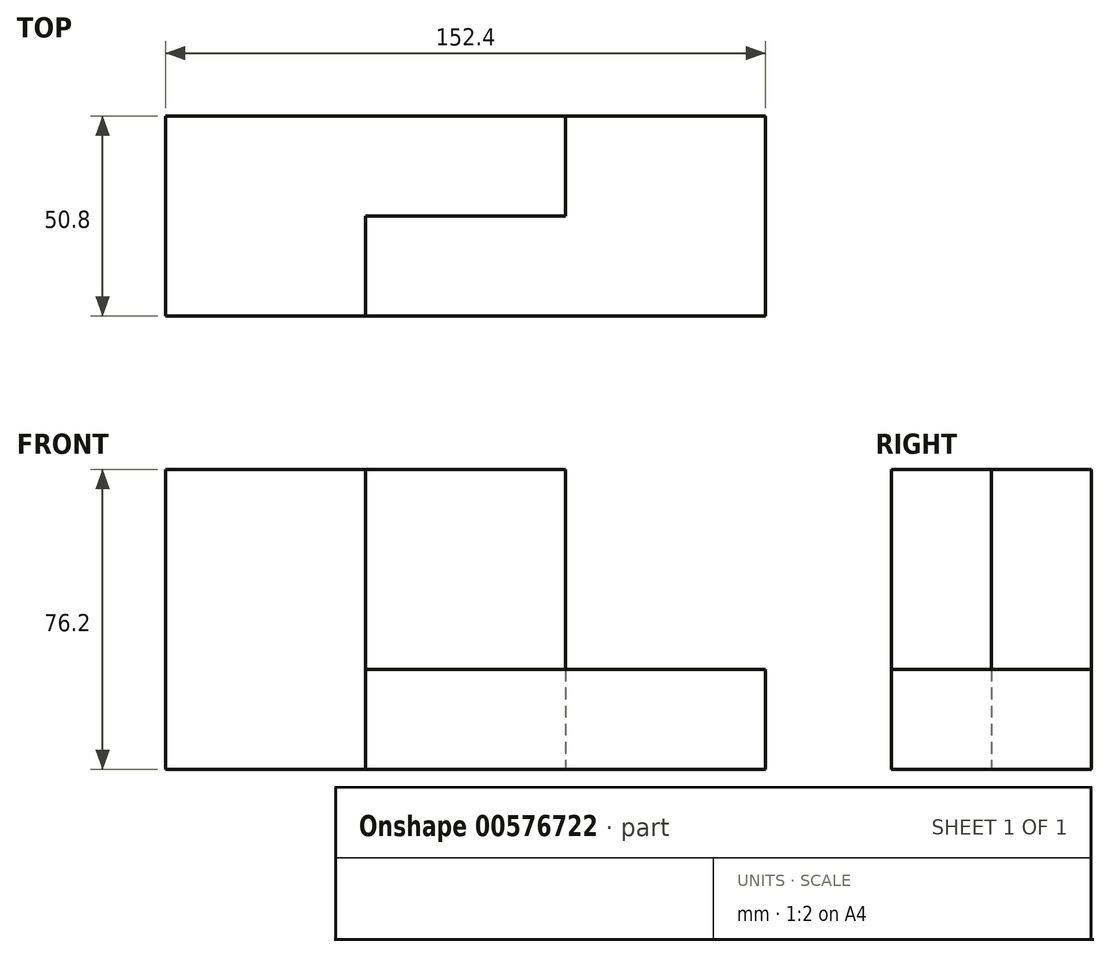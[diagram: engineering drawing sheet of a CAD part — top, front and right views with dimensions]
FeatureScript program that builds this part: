
annotation { "Feature Type Name" : "Feature", "Feature Type Description" : "" }
export const myFeature = defineFeature(function(context is Context, id is Id, definition is map)
    precondition{}
    {
        {
            var Q0;
            Q0=qCreatedBy(makeId("Top.planeOp"),FACE);
            var sketch = newSketch(context, id + "F0", { "sketchPlane" : qUnion([Q0])});
            skLineSegment(sketch, "E0.bottom", {"start": v(-43.4, 22.85) * mm, "end": v(109, 22.85) * mm});
            skLineSegment(sketch, "E0.top", {"start": v(-43.4, -27.95) * mm, "end": v(109, -27.95) * mm});
            skLineSegment(sketch, "E0.left", {"start": v(-43.4, 22.85) * mm, "end": v(-43.4, -27.95) * mm});
            skLineSegment(sketch, "E0.right", {"start": v(109, 22.85) * mm, "end": v(109, -27.95) * mm});
            skLineSegment(sketch, "E1", {"start": v(7.4, -27.95) * mm, "end": v(7.4, -2.55) * mm});
            skLineSegment(sketch, "E2", {"start": v(7.4, -2.55) * mm, "end": v(58.2, -2.55) * mm});
            skLineSegment(sketch, "E3", {"start": v(58.2, -2.55) * mm, "end": v(58.2, 22.85) * mm});
            skSolve(sketch);
        }
        {
            var Q0;
            {var subQ1=sQuery(id+"F0.wireOp",EDGE,"E0.left");Q0=makeQuery(id+"F0.imprint","IMPRINT",FACE,{"disambiguationData":[TD([[makeQuery(id+"F0.imprint","IMPRINT",EDGE,{"derivedFrom":subQ1}),1.0]])]});}
            extrude(context, id + "F1", {"entities" : qUnion([Q0]), "depth" : 76.2 * mm, "offsetDistance" : 25.4 * mm});
        }
        {
            var Q0;
            {var subQ0=sQuery(id+"F0.wireOp",EDGE,"E0.right");Q0=makeQuery(id+"F0.imprint","IMPRINT",FACE,{"disambiguationData":[TD([[makeQuery(id+"F0.imprint","IMPRINT",EDGE,{"derivedFrom":subQ0}),-1.0]])]});}
            extrude(context, id + "F2", {"entities" : qUnion([Q0]), "depth" : 25.4 * mm, "offsetDistance" : 25.4 * mm});
        }
    });
